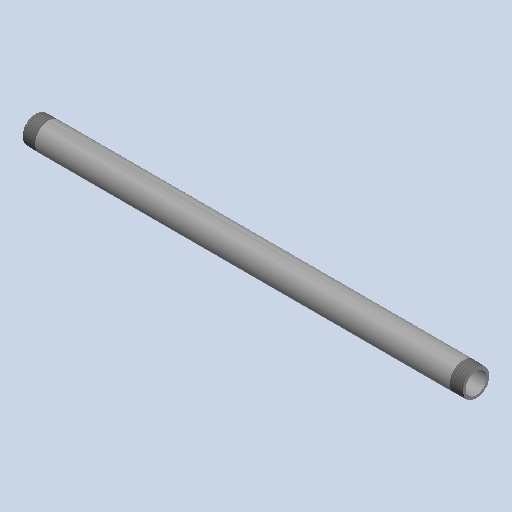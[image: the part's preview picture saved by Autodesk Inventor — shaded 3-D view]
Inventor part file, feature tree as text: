
AUTODESK INVENTOR PART (.ipt)
format: ipt  version: 2025 (Build 290162000, 162)  size: 175,104 bytes
history: native  units: mm (DEFAULTED — no unit token found)
features: other x8, revolve x1
ambient origin geometry x8: Origin, YZ Plane, XZ Plane, XY Plane, X Axis, Y Axis, Z Axis, Center Point
bodies: Solid1 (feature_tree)
feature tree (9):
  revolve  "Revolution1"  [1 undecoded]
  other  "Work Axis1"
  other  "Work Point5"
  other  "Work Axis2"
  other  "Work Point6"
  other  "Work Axis3"
  other  "Work Axis4"
  other  "Work Point7"
  other  "Work Point8"
note: 1 required parameter value undecoded (feature->parameter linkage not recoverable at this tier; creation-order binding heuristic only, values carry confidence <= 0.55)
